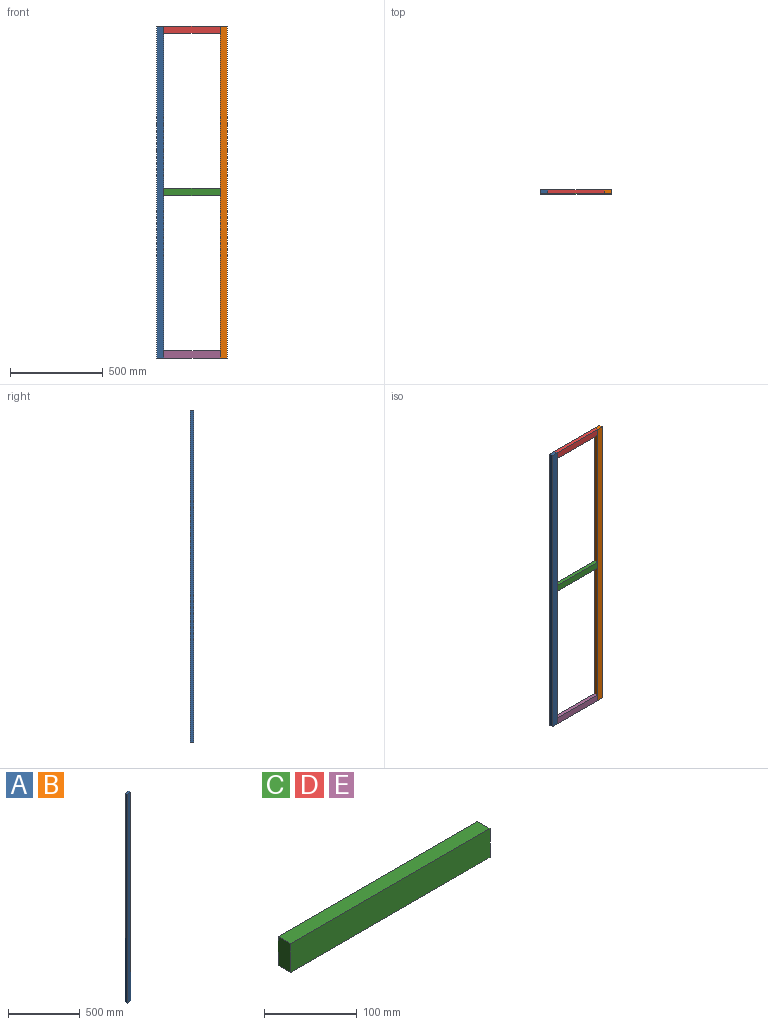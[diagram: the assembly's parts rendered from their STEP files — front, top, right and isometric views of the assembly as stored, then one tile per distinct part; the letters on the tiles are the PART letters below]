
ASSEMBLY  parts=5 mates=4
PART A: 6 faces, bbox 38.1x19.1x1786.1 mm
  f0: plane 1786.08x19.05mm, normal (1,0,0), area 34024.8mm2, adj f1,f3,f4,f5
  f1: plane 38.1x19.05mm, normal (0,0,1), area 725.8mm2, adj f0,f2,f4,f5
  f2: plane 1786.08x19.05mm, normal (-1,0,0), area 34024.8mm2, adj f1,f3,f4,f5
  f3: plane 38.1x19.05mm, normal (0,0,-1), area 725.8mm2, adj f0,f2,f4,f5
  f4: plane 1786.08x38.1mm, normal (0,-1,0), area 68049.6mm2, adj f0,f1,f2,f3
  f5: plane 1786.08x38.1mm, normal (0,1,0), area 68049.6mm2, adj f0,f1,f2,f3
PART B: same geometry as A
PART C: 6 faces, bbox 304.8x19.1x38.1 mm
  f0: plane 38.1x19.05mm, normal (-1,0,0), area 725.8mm2, adj f1,f3,f4,f5
  f1: plane 304.8x19.05mm, normal (0,0,-1), area 5806.4mm2, adj f0,f2,f4,f5
  f2: plane 38.1x19.05mm, normal (1,0,0), area 725.8mm2, adj f1,f3,f4,f5
  f3: plane 304.8x19.05mm, normal (0,0,1), area 5806.4mm2, adj f0,f2,f4,f5
  f4: plane 304.8x38.1mm, normal (0,-1,0), area 11612.9mm2, adj f0,f1,f2,f3
  f5: plane 304.8x38.1mm, normal (0,1,0), area 11612.9mm2, adj f0,f1,f2,f3
PART D: same geometry as C
PART E: same geometry as C
PLACE A t=(0,0,2.65)mm
PLACE B t=(342.9,0,2.65)mm
PLACE C t=(0,0,876.64)mm
PLACE D t=(0,0,1750.63)mm
PLACE E t=(0,0,2.65)mm
MATE fastened E.f4 <-> B.f4  axis (0,-1,0) through (1177.92,-2438.4,132.82)mm
MATE fastened B.f4 <-> D.f4  axis (0,-1,0) through (1177.92,-2438.4,1918.9)mm
MATE fastened B.f4 <-> C.f4  axis (0,-1,0) through (1177.92,-2438.4,1025.86)mm
MATE fastened A.f4 <-> E.f4  axis (0,-1,0) through (873.12,-2438.4,132.82)mm
